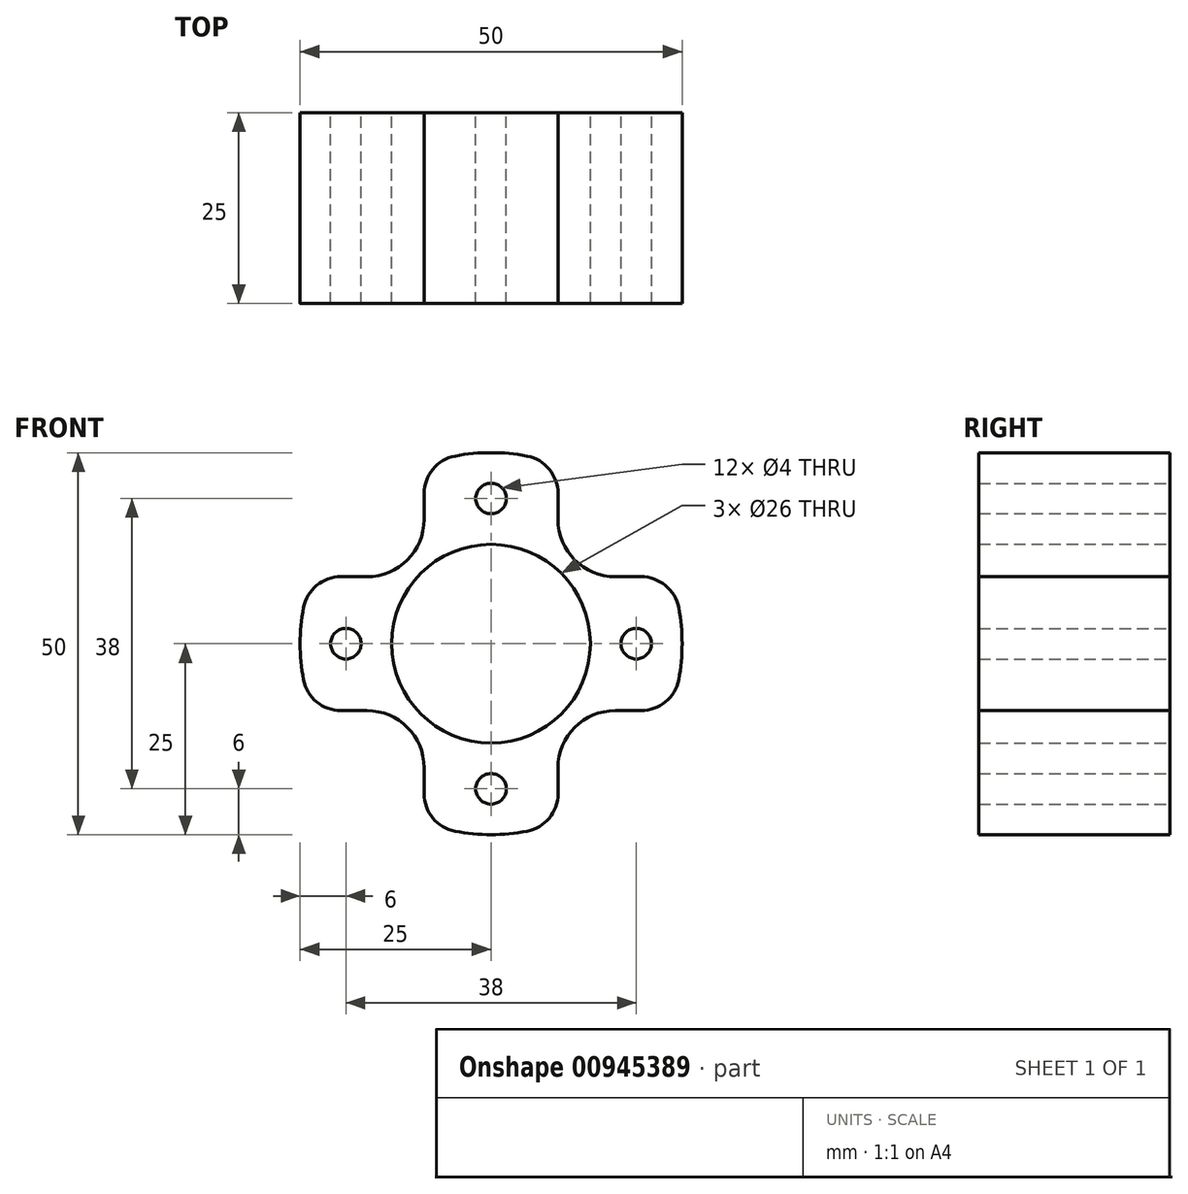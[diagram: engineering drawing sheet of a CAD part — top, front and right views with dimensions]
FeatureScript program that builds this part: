
annotation { "Feature Type Name" : "Feature", "Feature Type Description" : "" }
export const myFeature = defineFeature(function(context is Context, id is Id, definition is map)
    precondition{}
    {
        {
            var Q0;
            Q0=qCreatedBy(makeId("Front.planeOp"),FACE);
            var sketch = newSketch(context, id + "F0", { "sketchPlane" : qUnion([Q0])});
            skCircle(sketch, "E0", {"center": v(0, 0) * mm, "radius": 25 * mm});
            skCircle(sketch, "E1", {"center": v(0, 0) * mm, "radius": 13.5 * mm, "construction": true});
            skCircle(sketch, "E2", {"center": v(0, 19) * mm, "radius": 2 * mm});
            skCircle(sketch, "E3.MirrorC", {"center": v(0, -19) * mm, "radius": 2 * mm});
            skCircle(sketch, "E4", {"center": v(19, 0) * mm, "radius": 2 * mm});
            skCircle(sketch, "E5.MirrorC", {"center": v(-19, 0) * mm, "radius": 2 * mm});
            skSolve(sketch);
        }
        {
            var Q0;
            Q0=qSketchRegion(id+"F0",true);
            extrude(context, id + "F1", {"entities" : qUnion([Q0]), "depth" : 25 * mm, "offsetDistance" : 25 * mm});
        }
        {
            var Q0;
            Q0=qCreatedBy(makeId("Front.planeOp"),FACE);
            var sketch = newSketch(context, id + "F2", { "sketchPlane" : qUnion([Q0])});
            skPoint(sketch, "E6.middle", {"position": v(0, 0) * mm});
            skCircle(sketch, "E7", {"center": v(-16.26, 16.26) * mm, "radius": 2.5 * mm, "construction": true});
            skLineSegment(sketch, "E8", {"start": v(0, 0) * mm, "end": v(-39.56, 39.56) * mm, "construction": true});
            skLineSegment(sketch, "E9.bottom", {"start": v(-16.26, 8.76) * mm, "end": v(-23.76, 8.76) * mm});
            skLineSegment(sketch, "E9.top", {"start": v(-8.76, 23.76) * mm, "end": v(-23.76, 23.76) * mm});
            skLineSegment(sketch, "E9.left", {"start": v(-8.76, 16.26) * mm, "end": v(-8.76, 23.76) * mm});
            skLineSegment(sketch, "E9.right", {"start": v(-23.76, 8.76) * mm, "end": v(-23.76, 23.76) * mm});
            skPoint(sketch, "E10.visualSharp", {"position": v(-8.76, 8.76) * mm});
            skArc(sketch, "E10.filletArc", {"start": v(-16.26, 8.76) * mm, "mid": v(-10.96, 10.96) * mm, "end": v(-8.76, 16.26) * mm});
            skLineSegment(sketch, "E11.MirrorCS", {"start": v(8.76, 16.26) * mm, "end": v(8.76, 23.76) * mm});
            skArc(sketch, "E12.MirrorCS", {"start": v(16.26, 8.76) * mm, "mid": v(10.96, 10.96) * mm, "end": v(8.76, 16.26) * mm});
            skLineSegment(sketch, "E13.MirrorCS", {"start": v(16.26, 8.76) * mm, "end": v(23.76, 8.76) * mm});
            skLineSegment(sketch, "E14.MirrorCS", {"start": v(23.76, 8.76) * mm, "end": v(23.76, 23.76) * mm});
            skLineSegment(sketch, "E15.MirrorCS", {"start": v(8.76, 23.76) * mm, "end": v(23.76, 23.76) * mm});
            skLineSegment(sketch, "E16.MirrorCS", {"start": v(-16.26, -8.76) * mm, "end": v(-23.76, -8.76) * mm});
            skLineSegment(sketch, "E17.MirrorCS", {"start": v(-23.76, -8.76) * mm, "end": v(-23.76, -23.76) * mm});
            skLineSegment(sketch, "E18.MirrorCS", {"start": v(-8.76, -23.76) * mm, "end": v(-23.76, -23.76) * mm});
            skLineSegment(sketch, "E19.MirrorCS", {"start": v(-8.76, -16.26) * mm, "end": v(-8.76, -23.76) * mm});
            skArc(sketch, "E20.MirrorCS", {"start": v(-16.26, -8.76) * mm, "mid": v(-10.96, -10.96) * mm, "end": v(-8.76, -16.26) * mm});
            skLineSegment(sketch, "E21.MirrorCS", {"start": v(8.76, -16.26) * mm, "end": v(8.76, -23.76) * mm});
            skArc(sketch, "E22.MirrorCS", {"start": v(16.26, -8.76) * mm, "mid": v(10.96, -10.96) * mm, "end": v(8.76, -16.26) * mm});
            skLineSegment(sketch, "E23.MirrorCS", {"start": v(16.26, -8.76) * mm, "end": v(23.76, -8.76) * mm});
            skLineSegment(sketch, "E24.MirrorCS", {"start": v(23.76, -8.76) * mm, "end": v(23.76, -23.76) * mm});
            skLineSegment(sketch, "E25.MirrorCS", {"start": v(8.76, -23.76) * mm, "end": v(23.76, -23.76) * mm});
            skSolve(sketch);
        }
        {
            var Q0;
            Q0=makeQuery(id+"F2.imprint","IMPRINT",FACE,{"disambiguationData":[TD([[makeQuery(id+"F2.imprint","IMPRINT",EDGE,{"derivedFrom":sQuery(id+"F2.wireOp",EDGE,"E9.bottom")}),-1.0]])]});
            var Q1;
            Q1=makeQuery(id+"F2.imprint","IMPRINT",FACE,{"disambiguationData":[TD([[makeQuery(id+"F2.imprint","IMPRINT",EDGE,{"derivedFrom":sQuery(id+"F2.wireOp",EDGE,"E11.MirrorCS")}),-1.0]])]});
            var Q2;
            Q2=makeQuery(id+"F2.imprint","IMPRINT",FACE,{"disambiguationData":[TD([[makeQuery(id+"F2.imprint","IMPRINT",EDGE,{"derivedFrom":sQuery(id+"F2.wireOp",EDGE,"E16.MirrorCS")}),1.0]])]});
            var Q3;
            Q3=makeQuery(id+"F2.imprint","IMPRINT",FACE,{"disambiguationData":[TD([[makeQuery(id+"F2.imprint","IMPRINT",EDGE,{"derivedFrom":sQuery(id+"F2.wireOp",EDGE,"E21.MirrorCS")}),1.0]])]});
            extrude(context, id + "F3", {"entities" : qUnion([Q0, Q1, Q2, Q3]), "operationType" : NewBodyOperationType.REMOVE, "endBound" : BoundingType.THROUGH_ALL, "depth" : 25 * mm, "offsetDistance" : 25 * mm});
        }
        {
            var Q0;
            Q0=makeQuery(id+"F3.boolean.opBoolean","INTERSECT",EDGE,{"derivedFrom":[makeQuery(id+"F1.opExtrude","SWEPT_FACE",FACE,{"disambiguationData":[OSD([sQuery(id+"F0.wireOp",EDGE,"E0")])]}),makeQuery(id+"F3.opExtrude","SWEPT_FACE",FACE,{"disambiguationData":[OSD([sQuery(id+"F2.wireOp",EDGE,"E11.MirrorCS")])]})]});
            var Q1;
            Q1=makeQuery(id+"F3.boolean.opBoolean","INTERSECT",EDGE,{"derivedFrom":[makeQuery(id+"F1.opExtrude","SWEPT_FACE",FACE,{"disambiguationData":[OSD([sQuery(id+"F0.wireOp",EDGE,"E0")])]}),makeQuery(id+"F3.opExtrude","SWEPT_FACE",FACE,{"disambiguationData":[OSD([sQuery(id+"F2.wireOp",EDGE,"E9.left")])]})]});
            var Q2;
            Q2=makeQuery(id+"F3.boolean.opBoolean","INTERSECT",EDGE,{"derivedFrom":[makeQuery(id+"F1.opExtrude","SWEPT_FACE",FACE,{"disambiguationData":[OSD([sQuery(id+"F0.wireOp",EDGE,"E0")])]}),makeQuery(id+"F3.opExtrude","SWEPT_FACE",FACE,{"disambiguationData":[OSD([sQuery(id+"F2.wireOp",EDGE,"E9.bottom")])]})]});
            var Q3;
            Q3=makeQuery(id+"F3.boolean.opBoolean","INTERSECT",EDGE,{"derivedFrom":[makeQuery(id+"F1.opExtrude","SWEPT_FACE",FACE,{"disambiguationData":[OSD([sQuery(id+"F0.wireOp",EDGE,"E0")])]}),makeQuery(id+"F3.opExtrude","SWEPT_FACE",FACE,{"disambiguationData":[OSD([sQuery(id+"F2.wireOp",EDGE,"E16.MirrorCS")])]})]});
            var Q4;
            Q4=makeQuery(id+"F3.boolean.opBoolean","INTERSECT",EDGE,{"derivedFrom":[makeQuery(id+"F1.opExtrude","SWEPT_FACE",FACE,{"disambiguationData":[OSD([sQuery(id+"F0.wireOp",EDGE,"E0")])]}),makeQuery(id+"F3.opExtrude","SWEPT_FACE",FACE,{"disambiguationData":[OSD([sQuery(id+"F2.wireOp",EDGE,"E19.MirrorCS")])]})]});
            var Q5;
            Q5=makeQuery(id+"F3.boolean.opBoolean","INTERSECT",EDGE,{"derivedFrom":[makeQuery(id+"F1.opExtrude","SWEPT_FACE",FACE,{"disambiguationData":[OSD([sQuery(id+"F0.wireOp",EDGE,"E0")])]}),makeQuery(id+"F3.opExtrude","SWEPT_FACE",FACE,{"disambiguationData":[OSD([sQuery(id+"F2.wireOp",EDGE,"E21.MirrorCS")])]})]});
            var Q6;
            Q6=makeQuery(id+"F3.boolean.opBoolean","INTERSECT",EDGE,{"derivedFrom":[makeQuery(id+"F1.opExtrude","SWEPT_FACE",FACE,{"disambiguationData":[OSD([sQuery(id+"F0.wireOp",EDGE,"E0")])]}),makeQuery(id+"F3.opExtrude","SWEPT_FACE",FACE,{"disambiguationData":[OSD([sQuery(id+"F2.wireOp",EDGE,"E23.MirrorCS")])]})]});
            var Q7;
            Q7=makeQuery(id+"F3.boolean.opBoolean","INTERSECT",EDGE,{"derivedFrom":[makeQuery(id+"F1.opExtrude","SWEPT_FACE",FACE,{"disambiguationData":[OSD([sQuery(id+"F0.wireOp",EDGE,"E0")])]}),makeQuery(id+"F3.opExtrude","SWEPT_FACE",FACE,{"disambiguationData":[OSD([sQuery(id+"F2.wireOp",EDGE,"E13.MirrorCS")])]})]});
            fillet(context, id + "F4", {"entities" : qUnion([Q0, Q1, Q2, Q3, Q4, Q5, Q6, Q7]), "radius" : 5 * mm, "tangentPropagation" : true, "allowEdgeOverflow" : false});
        }
        {
            var Q0;
            Q0=qCreatedBy(makeId("Front.planeOp"),FACE);
            var sketch = newSketch(context, id + "F5", { "sketchPlane" : qUnion([Q0])});
            skCircle(sketch, "E26", {"center": v(0, 0) * mm, "radius": 13 * mm});
            skSolve(sketch);
        }
        {
            var Q0;
            Q0 = qSketchRegion(id + "F5", true);
            extrude(context, id + "F6", {"entities" : qUnion([Q0]), "operationType" : NewBodyOperationType.REMOVE, "endBound" : BoundingType.THROUGH_ALL, "depth" : 25 * mm, "offsetDistance" : 25 * mm});
        }
    });
